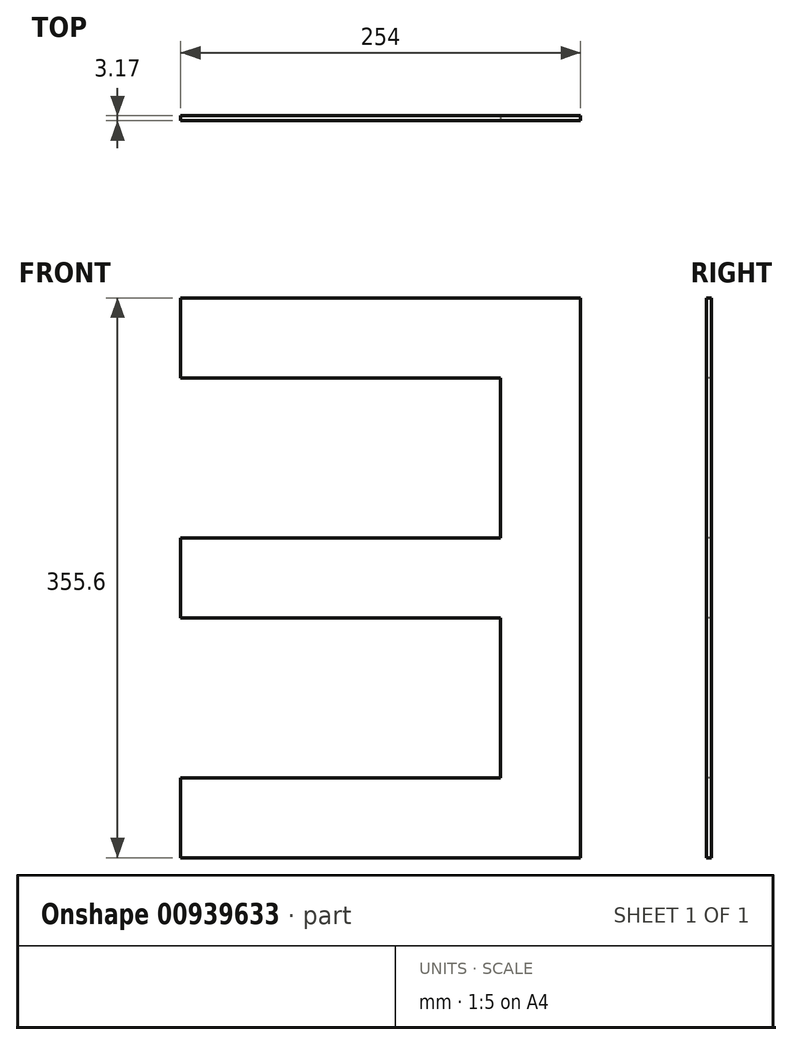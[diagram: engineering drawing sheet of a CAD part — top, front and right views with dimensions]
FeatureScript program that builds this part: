
annotation { "Feature Type Name" : "Feature", "Feature Type Description" : "" }
export const myFeature = defineFeature(function(context is Context, id is Id, definition is map)
    precondition{}
    {
        {
            var Q0;
            Q0=qCreatedBy(makeId("Front.planeOp"),FACE);
            var sketch = newSketch(context, id + "F0", { "sketchPlane" : qUnion([Q0])});
            skLineSegment(sketch, "E0.bottom", {"start": v(0, 0) * mm, "end": v(-50.8, 0) * mm});
            skLineSegment(sketch, "E0.top", {"start": v(0, 355.6) * mm, "end": v(-50.8, 355.6) * mm});
            skLineSegment(sketch, "E0.left", {"start": v(0, 0) * mm, "end": v(0, 355.6) * mm});
            skLineSegment(sketch, "E0.right", {"start": v(-50.8, 0) * mm, "end": v(-50.8, 355.6) * mm});
            skLineSegment(sketch, "E1.bottom", {"start": v(-50.8, 0) * mm, "end": v(-254, 0) * mm});
            skLineSegment(sketch, "E1.top", {"start": v(-50.8, 50.8) * mm, "end": v(-254, 50.8) * mm});
            skLineSegment(sketch, "E1.left", {"start": v(-50.8, 0) * mm, "end": v(-50.8, 50.8) * mm});
            skLineSegment(sketch, "E1.right", {"start": v(-254, 0) * mm, "end": v(-254, 50.8) * mm});
            skLineSegment(sketch, "E2.bottom", {"start": v(-50.8, 355.6) * mm, "end": v(-254, 355.6) * mm});
            skLineSegment(sketch, "E2.top", {"start": v(-50.8, 304.8) * mm, "end": v(-254, 304.8) * mm});
            skLineSegment(sketch, "E2.left", {"start": v(-50.8, 355.6) * mm, "end": v(-50.8, 304.8) * mm});
            skLineSegment(sketch, "E2.right", {"start": v(-254, 355.6) * mm, "end": v(-254, 304.8) * mm});
            skLineSegment(sketch, "E3.bottom", {"start": v(-50.8, 203.2) * mm, "end": v(-254, 203.2) * mm});
            skLineSegment(sketch, "E3.top", {"start": v(-50.8, 152.4) * mm, "end": v(-254, 152.4) * mm});
            skLineSegment(sketch, "E3.left", {"start": v(-50.8, 203.2) * mm, "end": v(-50.8, 152.4) * mm});
            skLineSegment(sketch, "E3.right", {"start": v(-254, 203.2) * mm, "end": v(-254, 152.4) * mm});
            skSolve(sketch);
        }
        {
            var Q0;
            Q0 = qSketchRegion(id + "F0", true);
            extrude(context, id + "F1", {"entities" : qUnion([Q0]), "oppositeDirection" : true, "depth" : 3.17 * mm, "offsetDistance" : 25.4 * mm});
        }
    });
